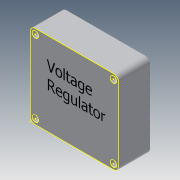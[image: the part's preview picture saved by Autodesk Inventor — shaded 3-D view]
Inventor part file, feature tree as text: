
AUTODESK INVENTOR PART (.ipt)
format: ipt  version: 2014 (Build 180170000, 170)  size: 99,840 bytes
history: native  units: in
note: dims shown in document units (in); Inventor stores cm internally (conversion verified against a paired STEP export)
features: sketch x2, extrude x1
ambient origin geometry x8: Origin, YZ Plane, XZ Plane, XY Plane, X Axis, Y Axis, Z Axis, Center Point
bodies: Solid1 (feature_tree)
feature tree (3):
  extrude  "Extrusion1"  Depth=2.0in
  sketch  "Sketch2"  dims[d2=0.125in d3=0.156in d4=0.75in d5=0.0in]
  sketch  "Sketch1"  dims[d0=2.125in d1=2.0in]
